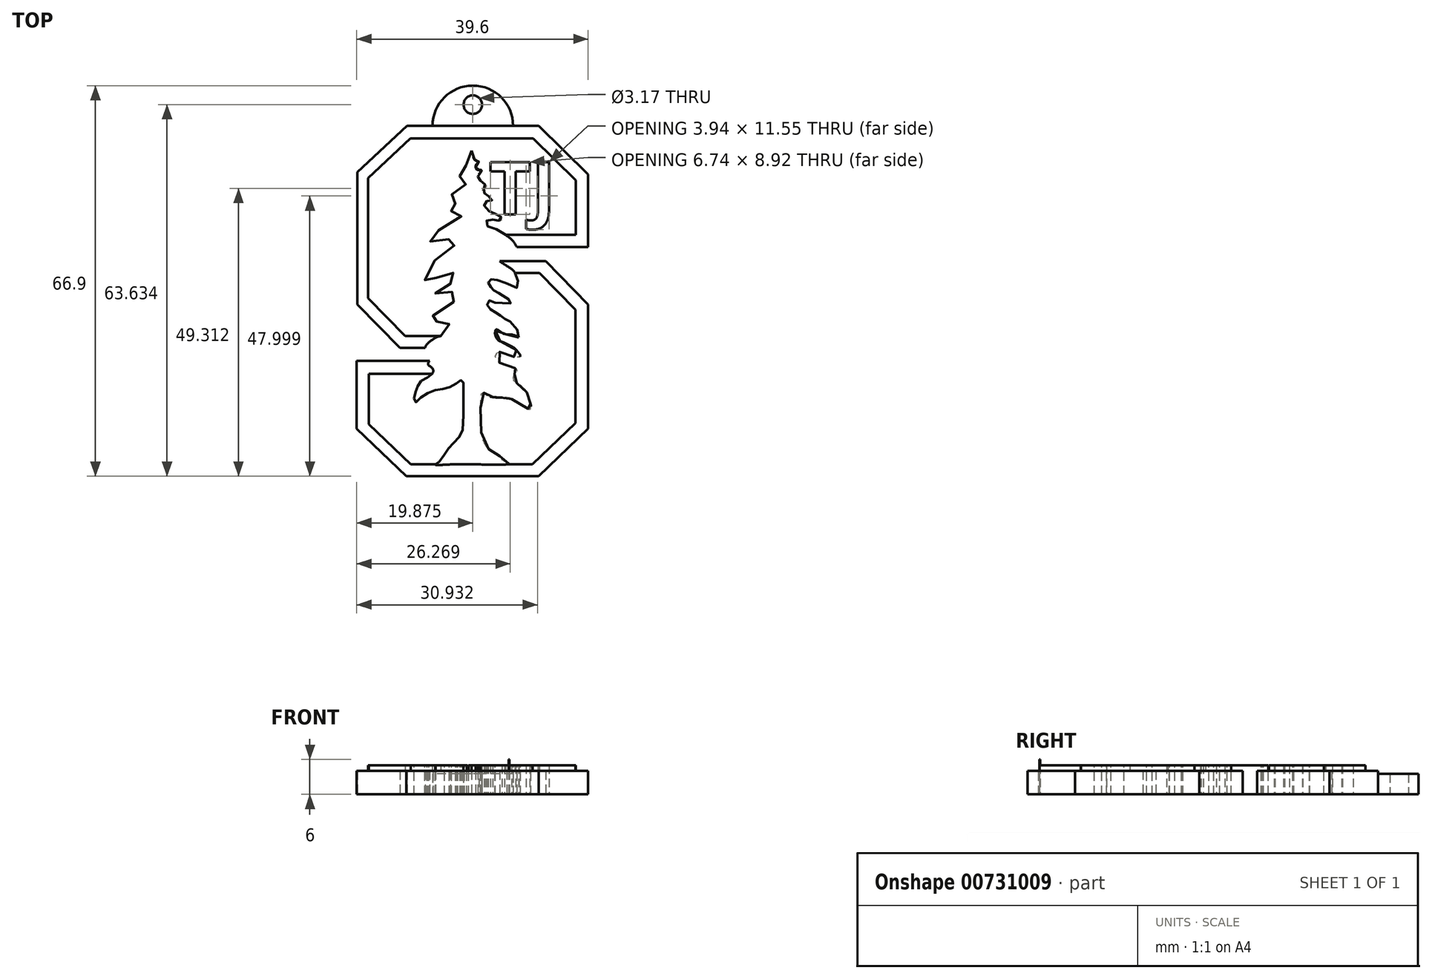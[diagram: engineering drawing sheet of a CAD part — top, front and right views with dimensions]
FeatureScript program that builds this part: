
annotation { "Feature Type Name" : "Feature", "Feature Type Description" : "" }
export const myFeature = defineFeature(function(context is Context, id is Id, definition is map)
    precondition{}
    {
        {
            var Q0;
            Q0=qCreatedBy(makeId("Top.planeOp"),FACE);
            var sketch = newSketch(context, id + "F0", { "sketchPlane" : qUnion([Q0])});
            skLineSegment(sketch, "E0", {"start": v(-26.5, 37.61) * mm, "end": v(-35.03, 29.67) * mm});
            skLineSegment(sketch, "E1", {"start": v(-35.03, 29.67) * mm, "end": v(-35.03, 6.99) * mm});
            skLineSegment(sketch, "E2", {"start": v(-35.03, 6.99) * mm, "end": v(-27.7, -0.43) * mm});
            skLineSegment(sketch, "E3", {"start": v(-23.83, -2.66) * mm, "end": v(-35.12, -2.66) * mm});
            skLineSegment(sketch, "E4", {"start": v(-35.12, -2.66) * mm, "end": v(-35.12, -14.26) * mm});
            skLineSegment(sketch, "E5", {"start": v(-35.12, -14.26) * mm, "end": v(-26.65, -22.39) * mm});
            skLineSegment(sketch, "E6", {"start": v(-26.65, -22.39) * mm, "end": v(-4, -22.39) * mm});
            skLineSegment(sketch, "E7", {"start": v(-4, -22.39) * mm, "end": v(4.48, -14.26) * mm});
            skLineSegment(sketch, "E8", {"start": v(4.48, -14.26) * mm, "end": v(4.48, 7.03) * mm});
            skLineSegment(sketch, "E9", {"start": v(4.48, 7.03) * mm, "end": v(-2.77, 14.43) * mm});
            skLineSegment(sketch, "E10", {"start": v(-2.77, 14.43) * mm, "end": v(-9.18, 14.43) * mm});
            skLineSegment(sketch, "E11", {"start": v(-6.9, 16.87) * mm, "end": v(4.48, 16.87) * mm});
            skLineSegment(sketch, "E12", {"start": v(4.48, 16.87) * mm, "end": v(4.48, 29.3) * mm});
            skLineSegment(sketch, "E13", {"start": v(4.48, 29.3) * mm, "end": v(-4, 37.61) * mm});
            skLineSegment(sketch, "E14", {"start": v(-4, 37.61) * mm, "end": v(-26.5, 37.61) * mm});
            skFitSpline(sketch, "E15", {"points": [v(-15.45, 33.35) * mm, v(-15.72, 32.35) * mm, v(-16.35, 31.4) * mm, v(-16.67, 31.22) * mm, v(-16.44, 30.81) * mm, v(-16.13, 30.6) * mm, v(-16, 30.1) * mm, v(-16.4, 29.53) * mm, v(-17.22, 29.08) * mm, v(-17.9, 28.63) * mm, v(-17.51, 28.35) * mm, v(-16.55, 28.28) * mm, v(-16.3, 27.77) * mm, v(-17, 27.38) * mm, v(-17.93, 26.93) * mm, v(-18.64, 26.32) * mm, v(-18.9, 25.88) * mm, v(-17.77, 25.88) * mm, v(-17.48, 25.5) * mm, v(-17.55, 24.69) * mm, v(-18.32, 24.27) * mm, v(-19.3, 23.76) * mm, v(-20.08, 23.09) * mm, v(-19.28, 22.99) * mm, v(-18.41, 23.09) * mm, v(-17.8, 23.18) * mm, v(-17.26, 23.02) * mm, v(-17.16, 22.44) * mm, v(-17.32, 22) * mm, v(-18.32, 21.35) * mm, v(-20.5, 20.13) * mm, v(-22.16, 18.98) * mm, v(-23.03, 18.08) * mm, v(-23, 17.63) * mm, v(-22.45, 17.86) * mm, v(-21.68, 17.98) * mm, v(-21.07, 17.86) * mm, v(-19.89, 18.05) * mm, v(-19.05, 18.37) * mm, v(-18.57, 18.79) * mm, v(-18.22, 18.47) * mm, v(-18.19, 17.6) * mm, v(-18.73, 16.73) * mm, v(-19.6, 15.93) * mm, v(-21.23, 14.92) * mm, v(-22.38, 14.06) * mm, v(-22.87, 13.12) * mm, v(-23.3, 11.87) * mm, v(-23.43, 10.51) * mm, v(-23.08, 10.72) * mm, v(-22.65, 11.16) * mm, v(-21.8, 11.5) * mm, v(-20.76, 11.73) * mm, v(-19.88, 11.77) * mm, v(-19.16, 12.17) * mm, v(-18.68, 12.4) * mm, v(-18.4, 12.42) * mm, v(-18.22, 12.15) * mm, v(-18.26, 11.62) * mm, v(-18.58, 11) * mm, v(-19.06, 10.57) * mm, v(-19.67, 10.23) * mm, v(-20.47, 9.83) * mm, v(-21.42, 9.27) * mm, v(-21.65, 8.83) * mm, v(-21.04, 8.68) * mm, v(-20.13, 8.7) * mm, v(-19.25, 8.95) * mm, v(-18.6, 9.33) * mm, v(-18.09, 9.48) * mm, v(-17.9, 9.16) * mm, v(-17.93, 8.28) * mm, v(-19.12, 6.98) * mm, v(-20.41, 6.18) * mm, v(-21.83, 5.32) * mm, v(-22.51, 4.64) * mm, v(-22.76, 4.1) * mm, v(-22.68, 3.93) * mm, v(-22.05, 4.18) * mm, v(-21.23, 4.07) * mm, v(-20.4, 4) * mm, v(-19.75, 4.03) * mm, v(-19.52, 4.1) * mm, v(-19.35, 3.87) * mm, v(-19.29, 3.53) * mm, v(-19.29, 3.17) * mm, v(-19.33, 2.94) * mm, v(-19.48, 2.4) * mm, v(-20.36, 1.76) * mm, v(-21.54, 1.38) * mm, v(-22.45, 0.78) * mm, v(-23, 0.33) * mm, v(-23.4, -0.38) * mm, v(-23.45, -0.8) * mm, v(-22.55, -0.68) * mm, v(-21.48, -0.34) * mm, v(-20.5, 0) * mm, v(-19.98, 0) * mm, v(-19.5, -0.15) * mm, v(-19.33, -0.7) * mm, v(-19.94, -1.62) * mm, v(-20.78, -2.2) * mm, v(-21.63, -2.48) * mm, v(-22.34, -2.5) * mm, v(-22.78, -2.78) * mm, v(-22.87, -3.3) * mm, v(-22.15, -3.93) * mm, v(-22.1, -4.65) * mm, v(-22.59, -5.24) * mm, v(-23.56, -5.78) * mm, v(-24.34, -6.27) * mm, v(-24.78, -7.17) * mm, v(-25.09, -8.05) * mm, v(-25.32, -9.02) * mm, v(-25.22, -9.6) * mm, v(-24.92, -9.7) * mm, v(-24.1, -8.87) * mm, v(-22.6, -8) * mm, v(-21.35, -7.59) * mm, v(-20.17, -7.42) * mm, v(-18.95, -7.05) * mm, v(-17.9, -6.39) * mm, v(-17.3, -5.97) * mm, v(-16.96, -5.97) * mm, v(-16.89, -6.86) * mm, v(-16.9, -13.73) * mm, v(-17.36, -15.4) * mm, v(-18.5, -16.67) * mm, v(-19.3, -17.56) * mm, v(-20.15, -18.78) * mm, v(-21, -19.9) * mm, v(-21.52, -20.21) * mm, v(-21.65, -20.42) * mm, v(-19.67, -20.4) * mm, v(-11.93, -20.4) * mm, v(-8.99, -20.37) * mm], "startDerivative": vector(-24.44, -119.75) * mm, "endDerivative": vector(180.95, 5.25) * mm});
            skFitSpline(sketch, "E16", {"points": [v(-8.99, -20.37) * mm, v(-9.52, -20) * mm, v(-10.23, -19.57) * mm, v(-10.42, -19.18) * mm, v(-10.9, -18.8) * mm, v(-11.5, -18.42) * mm, v(-12.27, -18.02) * mm, v(-12.86, -17.28) * mm, v(-13.55, -16.06) * mm, v(-13.9, -13.96) * mm, v(-13.91, -11.4) * mm, v(-13.83, -8.56) * mm, v(-13.68, -8.18) * mm, v(-13.43, -8.1) * mm, v(-13.15, -8.27) * mm, v(-12.84, -8.48) * mm, v(-12.38, -8.71) * mm, v(-11.98, -8.8) * mm, v(-11.66, -8.87) * mm, v(-11.47, -8.89) * mm, v(-10.95, -8.9) * mm, v(-10.6, -8.9) * mm, v(-10.46, -8.9) * mm, v(-9.7, -8.89) * mm, v(-9.62, -8.89) * mm, v(-8.99, -8.94) * mm, v(-8.57, -9.2) * mm, v(-8.28, -9.34) * mm, v(-7.96, -9.5) * mm, v(-7.5, -9.8) * mm, v(-7.1, -10.09) * mm, v(-6.78, -10.35) * mm, v(-6.38, -10.62) * mm, v(-6.01, -10.77) * mm, v(-5.77, -10.87) * mm, v(-5.56, -10.95) * mm, v(-5.4, -10.89) * mm, v(-5.35, -10.6) * mm, v(-5.33, -10.45) * mm, v(-5.33, -10.12) * mm, v(-5.5, -9.57) * mm, v(-5.6, -9.23) * mm, v(-5.84, -8.39) * mm, v(-6.2, -7.72) * mm, v(-6.57, -7.28) * mm, v(-7.5, -6.58) * mm, v(-8.19, -6.1) * mm, v(-8.3, -5.47) * mm, v(-8.26, -5.22) * mm, v(-8.15, -5.05) * mm, v(-7.9, -4.84) * mm, v(-7.8, -4.67) * mm, v(-7.67, -4.36) * mm, v(-7.65, -4.2) * mm, v(-7.88, -3.98) * mm, v(-8.34, -3.77) * mm, v(-9.52, -3.53) * mm, v(-11.16, -2.51) * mm, v(-11.4, -1.58) * mm, v(-10.93, -1.14) * mm, v(-10.11, -1.14) * mm, v(-9.35, -1.58) * mm, v(-8.05, -1.98) * mm, v(-7.08, -1.87) * mm, v(-7.35, -1.31) * mm, v(-8.04, -0.53) * mm, v(-9.54, 0.33) * mm, v(-10.76, 0.84) * mm, v(-11.09, 1.09) * mm, v(-11.41, 1.83) * mm, v(-11.37, 2.63) * mm, v(-11.07, 2.79) * mm, v(-10.34, 2.2) * mm, v(-9.24, 1.85) * mm, v(-8.5, 1.87) * mm, v(-7.77, 1.57) * mm, v(-7.43, 1.4) * mm], "startDerivative": vector(-35.1, 26.81) * mm, "endDerivative": vector(29.27, -14.04) * mm});
            skFitSpline(sketch, "E17", {"points": [v(-15.45, 33.35) * mm, v(-15.15, 32.37) * mm, v(-14.86, 31.74) * mm, v(-14.39, 31.53) * mm, v(-14.2, 31.51) * mm, v(-14.48, 31.19) * mm, v(-14.73, 30.94) * mm, v(-14.75, 30.46) * mm, v(-14.6, 30.14) * mm, v(-14.35, 30.08) * mm, v(-14.12, 30.06) * mm, v(-13.83, 30.04) * mm, v(-13.74, 29.99) * mm, v(-13.8, 29.78) * mm, v(-14.02, 29.5) * mm, v(-14.33, 29.26) * mm, v(-14.39, 29) * mm, v(-14.37, 28.7) * mm, v(-14.25, 28.48) * mm, v(-13.99, 28.25) * mm, v(-13.74, 28.02) * mm, v(-13.38, 27.77) * mm, v(-13.1, 27.52) * mm, v(-12.88, 27.3) * mm, v(-13.24, 26.82) * mm, v(-13.66, 26.53) * mm, v(-13.5, 26.23) * mm, v(-13.2, 26) * mm, v(-12.94, 25.85) * mm, v(-12.82, 25.75) * mm, v(-12.52, 25.56) * mm, v(-12.25, 25.26) * mm, v(-12.08, 25.06) * mm, v(-11.9, 24.84) * mm, v(-11.87, 24.72) * mm, v(-12.46, 24.66) * mm, v(-13.15, 24.68) * mm, v(-13.3, 24.27) * mm, v(-13.32, 23.96) * mm, v(-13.15, 23.54) * mm, v(-12.44, 23.02) * mm, v(-12.17, 22.9) * mm, v(-11.58, 22.64) * mm, v(-11.3, 22.5) * mm, v(-10.86, 22.24) * mm, v(-10.3, 21.9) * mm, v(-10.29, 21.54) * mm, v(-10.55, 21.42) * mm, v(-11.05, 21.4) * mm, v(-11.53, 21.55) * mm, v(-12.02, 21.55) * mm, v(-12.46, 21.52) * mm, v(-12.78, 21.4) * mm, v(-13.1, 21.23) * mm, v(-12.98, 20.62) * mm, v(-12.29, 20.32) * mm, v(-11.3, 19.93) * mm, v(-10.52, 19.53) * mm, v(-8.99, 18.47) * mm, v(-8.02, 17.4) * mm, v(-7.69, 16.54) * mm, v(-7.98, 16.58) * mm, v(-8.46, 16.67) * mm, v(-8.8, 16.71) * mm, v(-9.22, 16.73) * mm, v(-9.5, 16.75) * mm, v(-9.7, 16.8) * mm, v(-10.38, 16.94) * mm, v(-10.7, 16.98) * mm, v(-11.34, 17.05) * mm, v(-12.08, 17.32) * mm, v(-12.44, 17.53) * mm, v(-12.75, 17.13) * mm, v(-12.67, 16.73) * mm, v(-12.56, 16.42) * mm, v(-12.35, 16.06) * mm, v(-12, 15.7) * mm, v(-10.68, 14.44) * mm, v(-8.32, 12.84) * mm, v(-7.94, 12.15) * mm, v(-7.62, 11.37) * mm, v(-7.35, 10.24) * mm, v(-7.62, 9.9) * mm, v(-9.31, 10.55) * mm, v(-10.4, 10.93) * mm, v(-11.24, 11.24) * mm, v(-11.64, 11.33) * mm, v(-12, 11.35) * mm, v(-12.29, 11.26) * mm, v(-12.3, 11.24) * mm, v(-12.54, 11.05) * mm, v(-12.6, 10.7) * mm, v(-12.44, 10.38) * mm, v(-12.23, 10.05) * mm, v(-12.1, 9.88) * mm, v(-11.85, 9.63) * mm, v(-11.77, 9.56) * mm, v(-11.53, 9.4) * mm, v(-11.3, 9.3) * mm, v(-10.95, 9.02) * mm, v(-10.69, 8.9) * mm, v(-10.6, 8.83) * mm, v(-10.34, 8.68) * mm, v(-9.73, 8.36) * mm, v(-9.24, 8.05) * mm, v(-8.87, 7.73) * mm, v(-8.6, 7.42) * mm, v(-8.84, 7.2) * mm, v(-9.54, 7.27) * mm, v(-10.5, 7.21) * mm, v(-11.22, 7.21) * mm, v(-11.68, 7.5) * mm, v(-12.16, 7.65) * mm, v(-12.46, 7.69) * mm, v(-12.84, 7.54) * mm, v(-12.86, 7.1) * mm, v(-12.6, 6.58) * mm, v(-12.4, 6.32) * mm, v(-12.12, 6.1) * mm, v(-11.72, 5.92) * mm, v(-11.45, 5.72) * mm, v(-11, 5.38) * mm, v(-10.65, 5.2) * mm, v(-10.36, 5) * mm, v(-10.04, 4.79) * mm, v(-9.73, 4.56) * mm, v(-9.43, 4.45) * mm, v(-9, 4.2) * mm, v(-8.78, 3.97) * mm, v(-7.7, 2.75) * mm, v(-7.43, 1.68) * mm, v(-7.43, 1.4) * mm], "startDerivative": vector(27.53, -90.61) * mm, "endDerivative": vector(-1, -40.85) * mm});
            skLineSegment(sketch, "E18", {"start": v(-9.64, 18.96) * mm, "end": v(2.37, 18.96) * mm});
            skLineSegment(sketch, "E19", {"start": v(2.37, 18.96) * mm, "end": v(2.37, 28.3) * mm});
            skLineSegment(sketch, "E20", {"start": v(2.37, 28.3) * mm, "end": v(-4.9, 35.44) * mm});
            skLineSegment(sketch, "E21", {"start": v(-4.9, 35.44) * mm, "end": v(-25.95, 35.44) * mm});
            skLineSegment(sketch, "E22", {"start": v(-25.95, 35.44) * mm, "end": v(-33.2, 28.68) * mm});
            skLineSegment(sketch, "E23", {"start": v(-33.2, 28.68) * mm, "end": v(-33.2, 8.08) * mm});
            skLineSegment(sketch, "E24", {"start": v(-33.2, 8.08) * mm, "end": v(-26.84, 1.63) * mm});
            skLineSegment(sketch, "E25", {"start": v(-26.84, 1.63) * mm, "end": v(-20.73, 1.63) * mm});
            skLineSegment(sketch, "E26", {"start": v(-27.7, -0.43) * mm, "end": v(-23.43, -0.43) * mm});
            skLineSegment(sketch, "E27", {"start": v(-23.83, -2.66) * mm, "end": v(-22.67, -2.66) * mm});
            skLineSegment(sketch, "E28", {"start": v(-33.08, -4.85) * mm, "end": v(-22.2, -4.85) * mm});
            skLineSegment(sketch, "E29", {"start": v(-33.08, -4.85) * mm, "end": v(-33.08, -13.48) * mm});
            skLineSegment(sketch, "E30", {"start": v(-33.08, -13.48) * mm, "end": v(-25.9, -20.38) * mm});
            skLineSegment(sketch, "E31", {"start": v(2.33, -13.3) * mm, "end": v(-4.89, -20.22) * mm});
            skPoint(sketch, "E32.orphan", {"position": v(-3.64, -20.21) * mm});
            skLineSegment(sketch, "E33", {"start": v(-25.9, -20.38) * mm, "end": v(-5.05, -20.38) * mm});
            skLineSegment(sketch, "E34", {"start": v(-21.64, -20.35) * mm, "end": v(-21.67, -20.38) * mm});
            skLineSegment(sketch, "E35", {"start": v(-4.89, -20.22) * mm, "end": v(-5.05, -20.38) * mm});
            skLineSegment(sketch, "E36", {"start": v(2.33, -13.3) * mm, "end": v(2.33, 6.14) * mm});
            skLineSegment(sketch, "E37", {"start": v(2.33, 6.14) * mm, "end": v(-3.83, 12.43) * mm});
            skLineSegment(sketch, "E38", {"start": v(-3.83, 12.43) * mm, "end": v(-8.05, 12.43) * mm});
            skLineSegment(sketch, "E39", {"start": v(-9.18, 14.43) * mm, "end": v(-10.67, 14.43) * mm});
            skLineSegment(sketch, "E40", {"start": v(-6.9, 16.87) * mm, "end": v(-7.75, 16.87) * mm});
            skLineSegment(sketch, "E41", {"start": v(-9.14, -20.26) * mm, "end": v(-8.98, -20.38) * mm});
            skArc(sketch, "E42", {"start": v(-8.35, 37.61) * mm, "mid": v(-15.25, 44.51) * mm, "end": v(-22.15, 37.61) * mm});
            skCircle(sketch, "E43", {"center": v(-15.25, 41.24) * mm, "radius": 1.59 * mm});
            skText(sketch, "E44", { "text": "TJ", "fontName": "OpenSans-Bold.ttf"});
            const initialGuessF0  = {"E44": [-0.01247, 0.02246, 1, 0, 0.009]};
            skSetInitialGuess(sketch, initialGuessF0);
            skSolve(sketch);
        }
        {
            var Q0;
            {var subQ3=sQuery(id+"F0.wireOp",EDGE,"E16");Q0=makeQuery(id+"F0.imprint","IMPRINT",FACE,{"disambiguationData":[TD([[makeQuery(id+"F0.imprint","IMPRINT",EDGE,{"derivedFrom":subQ3}),-1.0]])]});}
            var Q1;
            {var subQ0=sQuery(id+"F0.wireOp",EDGE,"E18");Q1=makeQuery(id+"F0.imprint","IMPRINT",FACE,{"disambiguationData":[TD([[makeQuery(id+"F0.imprint","IMPRINT",EDGE,{"derivedFrom":subQ0}),1.0]])]});}
            var Q2;
            {var subQ1=sQuery(id+"F0.wireOp",EDGE,"E28");Q2=makeQuery(id+"F0.imprint","IMPRINT",FACE,{"disambiguationData":[TD([[makeQuery(id+"F0.imprint","IMPRINT",EDGE,{"derivedFrom":subQ1}),-1.0]])]});}
            extrude(context, id + "F1", {"entities" : qUnion([Q0, Q1, Q2]), "depth" : 5 * mm, "offsetDistance" : 25 * mm});
        }
        {
            var Q0;
            {var subQ7=sQuery(id+"F0.wireOp",EDGE,"E16");Q0=makeQuery(id+"F0.imprint","IMPRINT",FACE,{"disambiguationData":[TD([[makeQuery(id+"F0.imprint","IMPRINT",EDGE,{"derivedFrom":subQ7}),1.0]])]});}
            extrude(context, id + "F2", {"entities" : qUnion([Q0]), "operationType" : NewBodyOperationType.ADD, "depth" : 6 * mm, "offsetDistance" : 25 * mm});
        }
        {
            var Q0;
            Q0=makeQuery(id+"F0.imprint","IMPRINT",FACE,{"disambiguationData":[TD([[makeQuery(id+"F0.imprint","IMPRINT",EDGE,{"derivedFrom":sQuery(id+"F0.wireOp",EDGE,"E3")}),1.0]])]});
            var Q1;
            Q1=makeQuery(id+"F0.imprint","IMPRINT",FACE,{"disambiguationData":[TD([[makeQuery(id+"F0.imprint","IMPRINT",EDGE,{"derivedFrom":sQuery(id+"F0.wireOp",EDGE,"E0")}),1.0]])]});
            extrude(context, id + "F3", {"entities" : qUnion([Q0, Q1]), "operationType" : NewBodyOperationType.ADD, "depth" : 4 * mm, "offsetDistance" : 25 * mm});
        }
        {
            var Q0;
            {var subQ0=sQuery(id+"F0.wireOp",EDGE,"E42");Q0=makeQuery(id+"F0.imprint","IMPRINT",FACE,{"disambiguationData":[TD([[makeQuery(id+"F0.imprint","IMPRINT",EDGE,{"derivedFrom":subQ0}),1.0]])]});}
            extrude(context, id + "F4", {"entities" : qUnion([Q0]), "operationType" : NewBodyOperationType.ADD, "depth" : 3.5 * mm, "offsetDistance" : 25 * mm});
        }
    });
